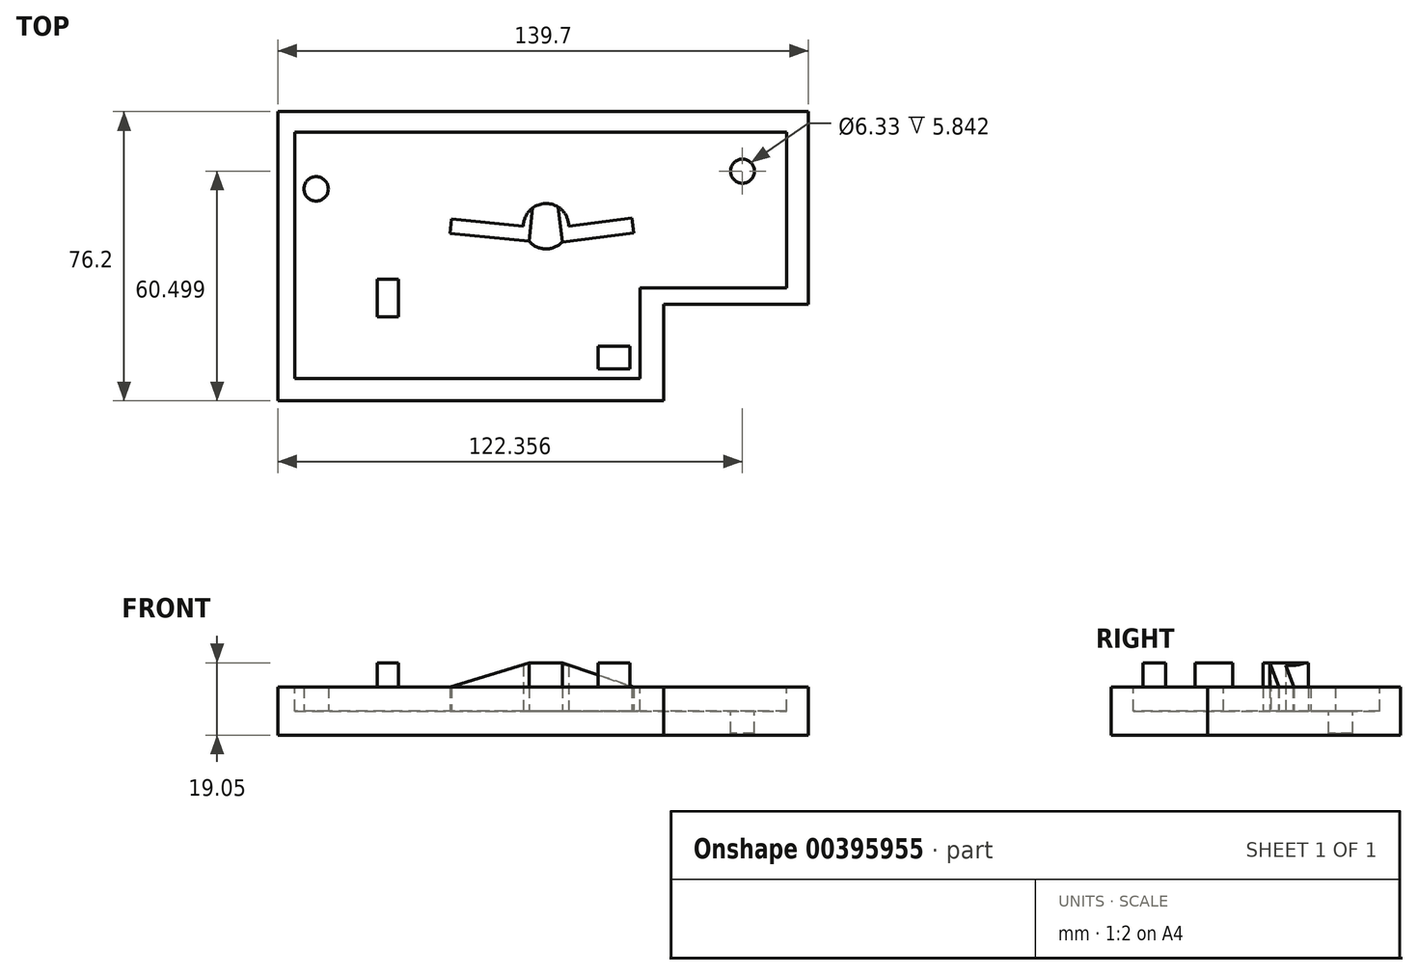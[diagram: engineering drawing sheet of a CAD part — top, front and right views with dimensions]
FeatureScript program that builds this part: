
annotation { "Feature Type Name" : "Feature", "Feature Type Description" : "" }
export const myFeature = defineFeature(function(context is Context, id is Id, definition is map)
    precondition{}
    {
        {
            var Q0;
            Q0=qCreatedBy(makeId("Top.planeOp"),FACE);
            var sketch = newSketch(context, id + "F0", { "sketchPlane" : qUnion([Q0])});
            skLineSegment(sketch, "E0.bottom", {"start": v(-70.63, 30.19) * mm, "end": v(69.07, 30.19) * mm});
            skLineSegment(sketch, "E0.top", {"start": v(-70.63, -46.01) * mm, "end": v(69.07, -46.01) * mm});
            skLineSegment(sketch, "E0.left", {"start": v(-70.63, 30.19) * mm, "end": v(-70.63, -46.01) * mm});
            skLineSegment(sketch, "E0.right", {"start": v(69.07, 30.19) * mm, "end": v(69.07, -46.01) * mm});
            skSolve(sketch);
        }
        {
            var Q0;
            Q0 = qSketchRegion(id + "F0", true);
            extrude(context, id + "F1", {"entities" : qUnion([Q0]), "depth" : 12.7 * mm});
        }
        {
            var Q0;
            Q0=makeQuery(id+"F1.opExtrude","CAP_FACE",FACE,{"disambiguationData":[OSD([sQuery(id+"F0.wireOp",EDGE,"E0.bottom"),sQuery(id+"F0.wireOp",EDGE,"E0.top"),sQuery(id+"F0.wireOp",EDGE,"E0.left"),sQuery(id+"F0.wireOp",EDGE,"E0.right")])],"isStart":false});
            var sketch = newSketch(context, id + "F2", { "sketchPlane" : qUnion([Q0])});
            skLineSegment(sketch, "E1.bottom", {"start": v(69.07, -46.01) * mm, "end": v(30.97, -46.01) * mm});
            skLineSegment(sketch, "E1.top", {"start": v(69.07, -20.61) * mm, "end": v(30.97, -20.61) * mm});
            skLineSegment(sketch, "E1.left", {"start": v(69.07, -46.01) * mm, "end": v(69.07, -20.61) * mm});
            skLineSegment(sketch, "E1.right", {"start": v(30.97, -46.01) * mm, "end": v(30.97, -20.61) * mm});
            skSolve(sketch);
        }
        {
            var Q0;
            Q0 = qSketchRegion(id + "F2", true);
            extrude(context, id + "F3", {"entities" : qUnion([Q0]), "operationType" : NewBodyOperationType.REMOVE, "oppositeDirection" : true, "depth" : 25.4 * mm});
        }
        {
            var Q0;
            Q0=makeQuery(id+"F1.opExtrude","CAP_FACE",FACE,{"disambiguationData":[OSD([sQuery(id+"F0.wireOp",EDGE,"E0.bottom"),sQuery(id+"F0.wireOp",EDGE,"E0.top"),sQuery(id+"F0.wireOp",EDGE,"E0.left"),sQuery(id+"F0.wireOp",EDGE,"E0.right")])],"isStart":false});
            var sketch = newSketch(context, id + "F4", { "sketchPlane" : qUnion([Q0])});
            skLineSegment(sketch, "E2", {"start": v(-66.2, 22.6) * mm, "end": v(-66.2, -40.16) * mm});
            skLineSegment(sketch, "E3", {"start": v(-66.2, -40.16) * mm, "end": v(24.79, -40.16) * mm});
            skLineSegment(sketch, "E4", {"start": v(24.79, -40.16) * mm, "end": v(24.79, -18.83) * mm});
            skLineSegment(sketch, "E5", {"start": v(24.79, -18.83) * mm, "end": v(24.79, -16.32) * mm});
            skLineSegment(sketch, "E6", {"start": v(24.79, -16.32) * mm, "end": v(63.38, -16.32) * mm});
            skLineSegment(sketch, "E7", {"start": v(63.38, -16.32) * mm, "end": v(63.38, 24.79) * mm});
            skLineSegment(sketch, "E8", {"start": v(63.38, 24.79) * mm, "end": v(-66.2, 24.79) * mm});
            skLineSegment(sketch, "E9", {"start": v(-66.2, 24.79) * mm, "end": v(-66.2, 22.6) * mm});
            skSolve(sketch);
        }
        {
            var Q0;
            Q0 = qSketchRegion(id + "F4", true);
            extrude(context, id + "F5", {"entities" : qUnion([Q0]), "operationType" : NewBodyOperationType.REMOVE, "oppositeDirection" : true, "depth" : 6.35 * mm});
        }
        {
            var Q0;
            Q0=makeQuery(id+"F5.boolean.opBoolean","COPY",FACE,{"derivedFrom":makeQuery(id+"F5.opExtrude","CAP_FACE",FACE,{"disambiguationData":[OSD([sQuery(id+"F4.wireOp",EDGE,"E2"),sQuery(id+"F4.wireOp",EDGE,"E3"),sQuery(id+"F4.wireOp",EDGE,"E4"),sQuery(id+"F4.wireOp",EDGE,"E5"),sQuery(id+"F4.wireOp",EDGE,"E6"),sQuery(id+"F4.wireOp",EDGE,"E7"),sQuery(id+"F4.wireOp",EDGE,"E8"),sQuery(id+"F4.wireOp",EDGE,"E9")])],"isStart":false})});
            var sketch = newSketch(context, id + "F6", { "sketchPlane" : qUnion([Q0])});
            skCircle(sketch, "E10", {"center": v(0, 0) * mm, "radius": 5.98 * mm});
            skSolve(sketch);
        }
        {
            var Q0;
            Q0 = qSketchRegion(id + "F6", true);
            extrude(context, id + "F7", {"entities" : qUnion([Q0]), "operationType" : NewBodyOperationType.ADD, "depth" : 12.7 * mm});
        }
        {
            var Q0;
            Q0=makeQuery(id+"F5.boolean.opBoolean","COPY",FACE,{"derivedFrom":makeQuery(id+"F5.opExtrude","CAP_FACE",FACE,{"disambiguationData":[OSD([sQuery(id+"F4.wireOp",EDGE,"E2"),sQuery(id+"F4.wireOp",EDGE,"E3"),sQuery(id+"F4.wireOp",EDGE,"E4"),sQuery(id+"F4.wireOp",EDGE,"E5"),sQuery(id+"F4.wireOp",EDGE,"E6"),sQuery(id+"F4.wireOp",EDGE,"E7"),sQuery(id+"F4.wireOp",EDGE,"E8"),sQuery(id+"F4.wireOp",EDGE,"E9")])],"isStart":false})});
            var sketch = newSketch(context, id + "F8", { "sketchPlane" : qUnion([Q0])});
            skLineSegment(sketch, "E11", {"start": v(-5.98, 0) * mm, "end": v(-24.88, 1.92) * mm});
            skLineSegment(sketch, "E12", {"start": v(-24.88, 1.92) * mm, "end": v(-25.27, -1.87) * mm});
            skLineSegment(sketch, "E13", {"start": v(-25.27, -1.87) * mm, "end": v(-4.45, -3.99) * mm});
            skLineSegment(sketch, "E14", {"start": v(-4.45, -3.99) * mm, "end": v(-5.98, 0) * mm});
            skLineSegment(sketch, "E15", {"start": v(5.98, 0) * mm, "end": v(22.54, 2.13) * mm});
            skLineSegment(sketch, "E16", {"start": v(22.54, 2.13) * mm, "end": v(23.04, -1.74) * mm});
            skLineSegment(sketch, "E17", {"start": v(23.04, -1.74) * mm, "end": v(4.3, -4.14) * mm});
            skLineSegment(sketch, "E18", {"start": v(4.3, -4.14) * mm, "end": v(5.98, 0) * mm});
            skSolve(sketch);
        }
        {
            var Q0;
            Q0 = qSketchRegion(id + "F8", true);
            extrude(context, id + "F9", {"entities" : qUnion([Q0]), "operationType" : NewBodyOperationType.ADD, "depth" : 12.7 * mm});
        }
        {
            var Q0;
            Q0=makeQuery(id+"F5.boolean.opBoolean","COPY",FACE,{"derivedFrom":makeQuery(id+"F5.opExtrude","CAP_FACE",FACE,{"disambiguationData":[OSD([sQuery(id+"F4.wireOp",EDGE,"E2"),sQuery(id+"F4.wireOp",EDGE,"E3"),sQuery(id+"F4.wireOp",EDGE,"E4"),sQuery(id+"F4.wireOp",EDGE,"E5"),sQuery(id+"F4.wireOp",EDGE,"E6"),sQuery(id+"F4.wireOp",EDGE,"E7"),sQuery(id+"F4.wireOp",EDGE,"E8"),sQuery(id+"F4.wireOp",EDGE,"E9")])],"isStart":false})});
            var sketch = newSketch(context, id + "F10", { "sketchPlane" : qUnion([Q0])});
            skCircle(sketch, "E19", {"center": v(51.73, 14.49) * mm, "radius": 3.17 * mm});
            skSolve(sketch);
        }
        {
            var Q0;
            Q0 = qSketchRegion(id + "F10", true);
            extrude(context, id + "F11", {"entities" : qUnion([Q0]), "operationType" : NewBodyOperationType.REMOVE, "oppositeDirection" : true, "depth" : 5.84 * mm});
        }
        {
            var Q0;
            Q0=makeQuery(id+"F5.boolean.opBoolean","COPY",FACE,{"derivedFrom":makeQuery(id+"F5.opExtrude","CAP_FACE",FACE,{"disambiguationData":[OSD([sQuery(id+"F4.wireOp",EDGE,"E2"),sQuery(id+"F4.wireOp",EDGE,"E3"),sQuery(id+"F4.wireOp",EDGE,"E4"),sQuery(id+"F4.wireOp",EDGE,"E5"),sQuery(id+"F4.wireOp",EDGE,"E6"),sQuery(id+"F4.wireOp",EDGE,"E7"),sQuery(id+"F4.wireOp",EDGE,"E8"),sQuery(id+"F4.wireOp",EDGE,"E9")])],"isStart":false})});
            var sketch = newSketch(context, id + "F12", { "sketchPlane" : qUnion([Q0])});
            skCircle(sketch, "E20", {"center": v(-60.55, 9.83) * mm, "radius": 3.2 * mm});
            skSolve(sketch);
        }
        {
            var Q0;
            Q0 = qSketchRegion(id + "F12", true);
            extrude(context, id + "F13", {"entities" : qUnion([Q0]), "operationType" : NewBodyOperationType.ADD, "depth" : 6.35 * mm});
        }
        {
            var Q0;
            Q0=makeQuery(id+"F9.opExtrude","SWEPT_FACE",FACE,{"disambiguationData":[OSD([sQuery(id+"F8.wireOp",EDGE,"E13")])]});
            var sketch = newSketch(context, id + "F14", { "sketchPlane" : qUnion([Q0])});
            skLineSegment(sketch, "E21", {"start": v(-4.02, 19.05) * mm, "end": v(-24.95, 12.7) * mm});
            skLineSegment(sketch, "E22", {"start": v(-24.95, 12.7) * mm, "end": v(-24.95, 19.05) * mm});
            skLineSegment(sketch, "E23", {"start": v(-24.95, 19.05) * mm, "end": v(-6.8, 19.05) * mm});
            skLineSegment(sketch, "E24", {"start": v(-6.8, 19.05) * mm, "end": v(-4.02, 19.05) * mm});
            skSolve(sketch);
        }
        {
            var Q0;
            Q0 = qSketchRegion(id + "F14", true);
            extrude(context, id + "F15", {"entities" : qUnion([Q0]), "operationType" : NewBodyOperationType.REMOVE, "oppositeDirection" : true, "depth" : 25.4 * mm});
        }
        {
            var Q0;
            Q0=makeQuery(id+"F9.opExtrude","SWEPT_FACE",FACE,{"disambiguationData":[OSD([sQuery(id+"F8.wireOp",EDGE,"E17")])]});
            var sketch = newSketch(context, id + "F16", { "sketchPlane" : qUnion([Q0])});
            skLineSegment(sketch, "E25", {"start": v(3.75, 19.05) * mm, "end": v(22.63, 12.7) * mm});
            skLineSegment(sketch, "E26", {"start": v(22.63, 12.7) * mm, "end": v(22.63, 19.05) * mm});
            skLineSegment(sketch, "E27", {"start": v(22.63, 19.05) * mm, "end": v(3.75, 19.05) * mm});
            skSolve(sketch);
        }
        {
            var Q0;
            Q0 = qSketchRegion(id + "F16", true);
            extrude(context, id + "F17", {"entities" : qUnion([Q0]), "operationType" : NewBodyOperationType.REMOVE, "oppositeDirection" : true, "depth" : 25.4 * mm});
        }
        {
            var Q0;
            Q0=makeQuery(id+"F4.imprint","IMPRINT",FACE,{"disambiguationData":[TD([[makeQuery(id+"F4.imprint","IMPRINT",EDGE,{"derivedFrom":sQuery(id+"F4.wireOp",EDGE,"E2")}),1.0]])]});
            var sketch = newSketch(context, id + "F18", { "sketchPlane" : qUnion([Q0])});
            skLineSegment(sketch, "E28.bottom", {"start": v(13.73, -31.65) * mm, "end": v(22.06, -31.65) * mm});
            skLineSegment(sketch, "E28.top", {"start": v(13.73, -37.53) * mm, "end": v(22.06, -37.53) * mm});
            skLineSegment(sketch, "E28.left", {"start": v(13.73, -31.65) * mm, "end": v(13.73, -37.53) * mm});
            skLineSegment(sketch, "E28.right", {"start": v(22.06, -31.65) * mm, "end": v(22.06, -37.53) * mm});
            skSolve(sketch);
        }
        {
            var Q0;
            Q0 = qSketchRegion(id + "F18", true);
            extrude(context, id + "F19", {"entities" : qUnion([Q0]), "depth" : 6.35 * mm});
        }
        {
            var Q0;
            Q0=makeQuery(id+"F4.imprint","IMPRINT",FACE,{"disambiguationData":[TD([[makeQuery(id+"F4.imprint","IMPRINT",EDGE,{"derivedFrom":sQuery(id+"F4.wireOp",EDGE,"E2")}),1.0]])]});
            var sketch = newSketch(context, id + "F20", { "sketchPlane" : qUnion([Q0])});
            skLineSegment(sketch, "E29.bottom", {"start": v(-44.46, -13.98) * mm, "end": v(-38.87, -13.98) * mm});
            skLineSegment(sketch, "E29.top", {"start": v(-44.46, -23.83) * mm, "end": v(-38.87, -23.83) * mm});
            skLineSegment(sketch, "E29.left", {"start": v(-44.46, -13.98) * mm, "end": v(-44.46, -23.83) * mm});
            skLineSegment(sketch, "E29.right", {"start": v(-38.87, -13.98) * mm, "end": v(-38.87, -23.83) * mm});
            skSolve(sketch);
        }
        {
            var Q0;
            Q0 = qSketchRegion(id + "F20", true);
            extrude(context, id + "F21", {"entities" : qUnion([Q0]), "depth" : 6.35 * mm});
        }
    });
